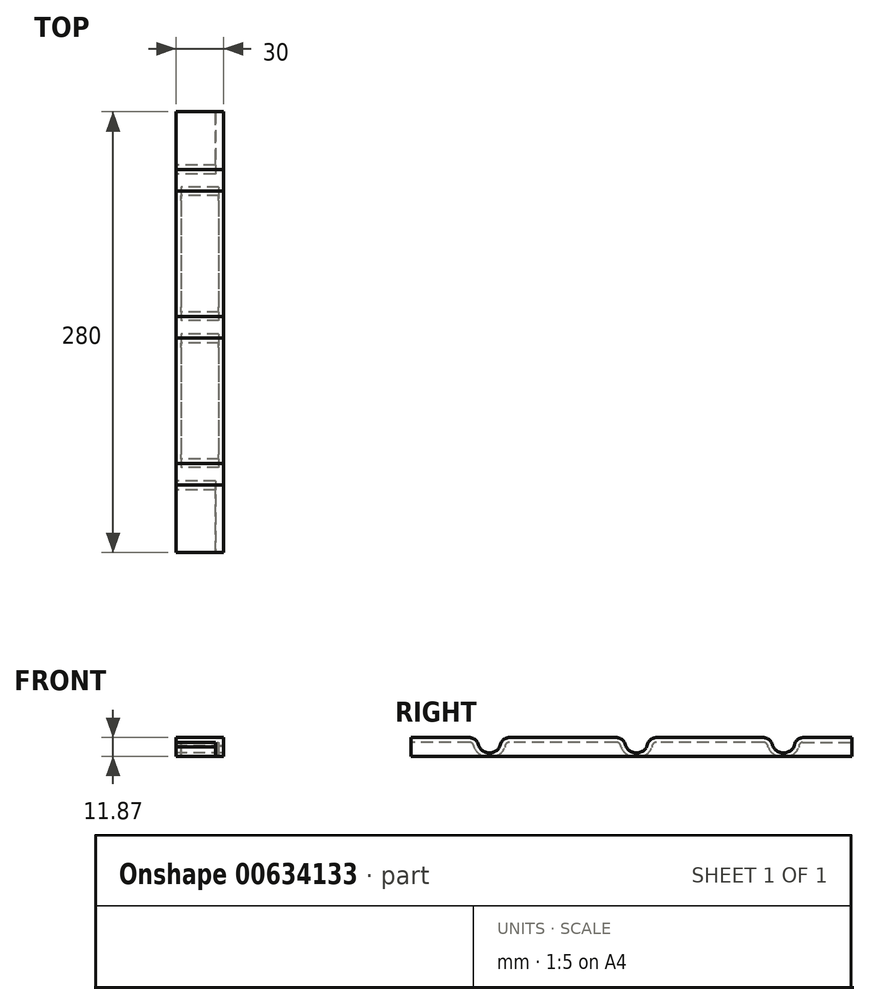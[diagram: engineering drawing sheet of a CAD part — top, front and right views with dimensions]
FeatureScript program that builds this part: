
annotation { "Feature Type Name" : "Feature", "Feature Type Description" : "" }
export const myFeature = defineFeature(function(context is Context, id is Id, definition is map)
    precondition{}
    {
        {
            var Q0;
            Q0=qCreatedBy(makeId("Front.planeOp"),FACE);
            var sketch = newSketch(context, id + "F0", { "sketchPlane" : qUnion([Q0])});
            skLineSegment(sketch, "E0.bottom", {"start": v(-15, 40) * mm, "end": v(15, 40) * mm});
            skLineSegment(sketch, "E0.top", {"start": v(-12, 0) * mm, "end": v(12, 0) * mm});
            skLineSegment(sketch, "E0.left", {"start": v(-15, 40) * mm, "end": v(-15, 37) * mm});
            skLineSegment(sketch, "E0.right", {"start": v(15, 37) * mm, "end": v(15, 3) * mm});
            skLineSegment(sketch, "E1.0", {"start": v(-15, 37) * mm, "end": v(3, 37) * mm});
            skLineSegment(sketch, "E1.1", {"start": v(-12, 6) * mm, "end": v(-12, 6) * mm});
            skLineSegment(sketch, "E1.2", {"start": v(-9, 3) * mm, "end": v(9, 3) * mm});
            skLineSegment(sketch, "E1.3", {"start": v(12, 29.6) * mm, "end": v(12, 6) * mm});
            skLineSegment(sketch, "E2.0", {"start": v(-15, 6) * mm, "end": v(-12, 6) * mm});
            skLineSegment(sketch, "E3", {"start": v(12, 40) * mm, "end": v(7.5, 40) * mm, "construction": true});
            skLineSegment(sketch, "E4", {"start": v(7, 34.8) * mm, "end": v(7, 40) * mm, "construction": true});
            skArc(sketch, "E5", {"start": v(7, 40) * mm, "mid": v(6.75, 29.6) * mm, "end": v(7.5, 39.98) * mm});
            skLineSegment(sketch, "E6.trimOffspring", {"start": v(-15, 6) * mm, "end": v(-15, 3) * mm});
            skPoint(sketch, "E7.orphan", {"position": v(5, 29.7) * mm});
            skPoint(sketch, "E8.visualSharp", {"position": v(15, 40) * mm});
            skArc(sketch, "E8.filletArc", {"start": v(15, 37) * mm, "mid": v(14.12, 39.12) * mm, "end": v(12, 40) * mm});
            skPoint(sketch, "E9.visualSharp", {"position": v(15, 0) * mm});
            skArc(sketch, "E9.filletArc", {"start": v(12, 0) * mm, "mid": v(14.12, 0.88) * mm, "end": v(15, 3) * mm});
            skArc(sketch, "E10.filletArc", {"start": v(9, 3) * mm, "mid": v(11.12, 3.88) * mm, "end": v(12, 6) * mm});
            skPoint(sketch, "E11.visualSharp", {"position": v(-12, 3) * mm});
            skArc(sketch, "E11.filletArc", {"start": v(-12, 6) * mm, "mid": v(-11.12, 3.88) * mm, "end": v(-9, 3) * mm});
            skPoint(sketch, "E12.visualSharp", {"position": v(-15, 0) * mm});
            skArc(sketch, "E12.filletArc", {"start": v(-15, 3) * mm, "mid": v(-14.12, 0.88) * mm, "end": v(-12, 0) * mm});
            skLineSegment(sketch, "E13.0", {"start": v(6.5, 34.8) * mm, "end": v(6.5, 39.8) * mm});
            skLineSegment(sketch, "E14.0", {"start": v(7.5, 34.8) * mm, "end": v(7.5, 40) * mm});
            skLineSegment(sketch, "E15", {"start": v(-15, 6) * mm, "end": v(-15, 16) * mm});
            skLineSegment(sketch, "E16", {"start": v(-15, 16) * mm, "end": v(-12, 16) * mm});
            skLineSegment(sketch, "E17", {"start": v(-12, 16) * mm, "end": v(-12, 6) * mm});
            skLineSegment(sketch, "E18", {"start": v(6.75, 29.6) * mm, "end": v(12, 29.6) * mm});
            skSolve(sketch);
        }
        {
            var Q0;
            Q0=qCreatedBy(makeId("Front.planeOp"),FACE);
            var sketch = newSketch(context, id + "F1", { "sketchPlane" : qUnion([Q0])});
            skArc(sketch, "E19.0.0", {"start": v(7.25, 29.6) * mm, "mid": v(12.2, 34.67) * mm, "end": v(7.5, 39.98) * mm});
            skLineSegment(sketch, "E19.0.1", {"start": v(7.5, 39.98) * mm, "end": v(7.5, 40) * mm});
            skArc(sketch, "E19.0.3", {"start": v(6.5, 39.98) * mm, "mid": v(4, 39.05) * mm, "end": v(2.29, 37) * mm});
            skArc(sketch, "E19.0.4", {"start": v(2.29, 37) * mm, "mid": v(2.55, 32.11) * mm, "end": v(6.75, 29.6) * mm});
            skLineSegment(sketch, "E19.0.5", {"start": v(6.75, 29.6) * mm, "end": v(7.25, 29.6) * mm});
            skArc(sketch, "E19.1.0", {"start": v(2.29, 37) * mm, "mid": v(4, 39.05) * mm, "end": v(6.5, 39.98) * mm});
            skLineSegment(sketch, "E19.1.1", {"start": v(6.5, 40) * mm, "end": v(-15, 40) * mm});
            skLineSegment(sketch, "E19.1.2", {"start": v(-15, 40) * mm, "end": v(-15, 37) * mm});
            skLineSegment(sketch, "E19.1.3", {"start": v(-15, 37) * mm, "end": v(-0.9, 37) * mm});
            skArc(sketch, "E19.2.0", {"start": v(7.5, 39.98) * mm, "mid": v(12.2, 34.67) * mm, "end": v(7.25, 29.6) * mm});
            skLineSegment(sketch, "E19.2.2", {"start": v(12, 26.6) * mm, "end": v(12, 25) * mm});
            skArc(sketch, "E19.2.3", {"start": v(12, 6) * mm, "mid": v(11.12, 3.88) * mm, "end": v(9, 3) * mm, "construction": true});
            skLineSegment(sketch, "E19.2.4", {"start": v(9, 3) * mm, "end": v(-9, 3) * mm, "construction": true});
            skArc(sketch, "E19.2.5", {"start": v(-9, 3) * mm, "mid": v(-11.12, 3.88) * mm, "end": v(-12, 6) * mm, "construction": true});
            skLineSegment(sketch, "E19.2.7", {"start": v(-15, 6) * mm, "end": v(-15, 3) * mm, "construction": true});
            skArc(sketch, "E19.2.8", {"start": v(-15, 3) * mm, "mid": v(-14.12, 0.88) * mm, "end": v(-12, 0) * mm, "construction": true});
            skLineSegment(sketch, "E19.2.9", {"start": v(-12, 0) * mm, "end": v(12, 0) * mm, "construction": true});
            skArc(sketch, "E19.2.10", {"start": v(12, 0) * mm, "mid": v(14.12, 0.88) * mm, "end": v(15, 3) * mm, "construction": true});
            skLineSegment(sketch, "E19.2.11", {"start": v(15, 22) * mm, "end": v(15, 37) * mm});
            skArc(sketch, "E19.2.12", {"start": v(15, 37) * mm, "mid": v(14.12, 39.12) * mm, "end": v(12, 40) * mm});
            skLineSegment(sketch, "E19.2.13", {"start": v(12, 40) * mm, "end": v(7.5, 40) * mm});
            skLineSegment(sketch, "E19.2.14", {"start": v(7.5, 40) * mm, "end": v(7.5, 39.98) * mm});
            skLineSegment(sketch, "E19.3.0", {"start": v(-15, 28.87) * mm, "end": v(-15, 20) * mm});
            skLineSegment(sketch, "E19.3.2", {"start": v(-12, 23) * mm, "end": v(-12, 28.87) * mm});
            skLineSegment(sketch, "E19.3.3", {"start": v(-12, 16) * mm, "end": v(-12, 16) * mm});
            skPoint(sketch, "E20.2", {"position": v(6.5, 37.3) * mm});
            skPoint(sketch, "E21.orphan", {"position": v(6.5, 39.8) * mm});
            skPoint(sketch, "E19.0.2.end.orphan", {"position": v(7, 40) * mm});
            skArc(sketch, "E22.0", {"start": v(-0.9, 37) * mm, "mid": v(0.38, 29.97) * mm, "end": v(6.69, 26.6) * mm});
            skLineSegment(sketch, "E23.0", {"start": v(9.25, 26.6) * mm, "end": v(12, 26.6) * mm});
            skLineSegment(sketch, "E24.0", {"start": v(6.69, 26.6) * mm, "end": v(9.25, 26.6) * mm});
            skPoint(sketch, "E25.orphan", {"position": v(12, 29.6) * mm});
            skLineSegment(sketch, "E26.trimOffspring", {"start": v(6.5, 39.98) * mm, "end": v(6.5, 40) * mm});
            skPoint(sketch, "E27.orphan", {"position": v(7.5, 34.8) * mm});
            skPoint(sketch, "E20.0.start.orphan", {"position": v(6.5, 34.8) * mm});
            skLineSegment(sketch, "E28", {"start": v(7, 20) * mm, "end": v(-9, 20) * mm});
            skPoint(sketch, "E28.endSnap0", {"position": v(15, 20) * mm});
            skLineSegment(sketch, "E29", {"start": v(-15, 28.87) * mm, "end": v(-12, 28.87) * mm});
            skPoint(sketch, "E30.orphan", {"position": v(-15.47, 20) * mm});
            skLineSegment(sketch, "E31.0", {"start": v(10, 17) * mm, "end": v(-12, 17) * mm});
            skPoint(sketch, "E32.visualSharp", {"position": v(12, 20) * mm});
            skArc(sketch, "E32.filletArc", {"start": v(7, 20) * mm, "mid": v(10.54, 21.46) * mm, "end": v(12, 25) * mm});
            skPoint(sketch, "E33.visualSharp", {"position": v(15, 17) * mm});
            skArc(sketch, "E33.filletArc", {"start": v(10, 17) * mm, "mid": v(13.54, 18.46) * mm, "end": v(15, 22) * mm});
            skPoint(sketch, "E34.visualSharp", {"position": v(-15, 16) * mm});
            skPoint(sketch, "E35.visualSharp", {"position": v(-12, 20) * mm});
            skArc(sketch, "E35.filletArc", {"start": v(-12, 23) * mm, "mid": v(-11.12, 20.88) * mm, "end": v(-9, 20) * mm});
            skPoint(sketch, "E36.visualSharp", {"position": v(-15, 17) * mm});
            skArc(sketch, "E36.filletArc", {"start": v(-15, 20) * mm, "mid": v(-14.12, 17.88) * mm, "end": v(-12, 17) * mm});
            skSolve(sketch);
        }
        {
            var Q0;
            Q0=qCreatedBy(makeId("Front.planeOp"),FACE);
            var sketch = newSketch(context, id + "F2", { "sketchPlane" : qUnion([Q0])});
            skLineSegment(sketch, "E37", {"start": v(-15, 28.87) * mm, "end": v(-45, 28.87) * mm});
            skLineSegment(sketch, "E38", {"start": v(-45, 28.87) * mm, "end": v(-45, 17) * mm});
            skLineSegment(sketch, "E39.0", {"start": v(-15, 17) * mm, "end": v(-45, 17) * mm});
            skPoint(sketch, "E40.orphan", {"position": v(-12, 17) * mm});
            skLineSegment(sketch, "E41", {"start": v(-15, 28.87) * mm, "end": v(-15, 17) * mm});
            skPoint(sketch, "E42.orphan", {"position": v(10, 17) * mm});
            skSolve(sketch);
        }
        {
            var Q0;
            Q0 = qSketchRegion(id + "F2", true);
            extrude(context, id + "F3", {"entities" : qUnion([Q0]), "oppositeDirection" : true, "depth" : 280 * mm, "offsetDistance" : 25 * mm});
        }
        {
            var Q0;
            Q0=makeQuery(id+"F3.opExtrude","SWEPT_FACE",FACE,{"disambiguationData":[OSD([sQuery(id+"F2.wireOp",EDGE,"E38")])]});
            var sketch = newSketch(context, id + "F4", { "sketchPlane" : qUnion([Q0])});
            skSolve(sketch);
        }
        {
            var Q0;
            {var subQ0=sQuery(id+"F2.wireOp",EDGE,"E38");Q0=makeQuery(id+"F4.imprint","IMPRINT",FACE,{"disambiguationData":[TD([[makeQuery(id+"F4.imprint","IMPRINT",EDGE,{"derivedFrom":makeQuery(id+"F3.opExtrude","CAP_EDGE",EDGE,{"disambiguationData":[OSD([subQ0])],"isStart":true})}),-1.0]])]});}
            var sketch = newSketch(context, id + "F5", { "sketchPlane" : qUnion([Q0])});
            skLineSegment(sketch, "E43.0", {"start": v(-280, 17) * mm, "end": v(0, 17) * mm, "construction": true});
            skLineSegment(sketch, "E44.0", {"start": v(-280, 24) * mm, "end": v(0, 24) * mm, "construction": true});
            skSolve(sketch);
        }
        {
            var Q0;
            {var subQ0=sQuery(id+"F2.wireOp",EDGE,"E38");Q0=makeQuery(id+"F4.imprint","IMPRINT",FACE,{"disambiguationData":[TD([[makeQuery(id+"F4.imprint","IMPRINT",EDGE,{"derivedFrom":makeQuery(id+"F3.opExtrude","CAP_EDGE",EDGE,{"disambiguationData":[OSD([subQ0])],"isStart":true})}),-1.0]])]});}
            var sketch = newSketch(context, id + "F6", { "sketchPlane" : qUnion([Q0])});
            skLineSegment(sketch, "E45", {"start": v(0, 16.97) * mm, "end": v(-42.76, 16.97) * mm, "construction": true});
            skLineSegment(sketch, "E46", {"start": v(-42.76, 16.97) * mm, "end": v(-42.76, 25.5) * mm, "construction": true});
            skLineSegment(sketch, "E47", {"start": v(-42.76, 25.5) * mm, "end": v(-56.43, 25.5) * mm, "construction": true});
            skLineSegment(sketch, "E48", {"start": v(-56.43, 25.5) * mm, "end": v(-56.43, 16.97) * mm, "construction": true});
            skArc(sketch, "E49", {"start": v(-42.76, 25.5) * mm, "mid": v(-49.6, 28.8) * mm, "end": v(-56.43, 25.5) * mm, "construction": true});
            skLineSegment(sketch, "E50", {"start": v(-42.76, 16.97) * mm, "end": v(-42.76, 7.64) * mm, "construction": true});
            skLineSegment(sketch, "E51", {"start": v(-42.76, 7.64) * mm, "end": v(-57.13, 7.64) * mm, "construction": true});
            skLineSegment(sketch, "E52", {"start": v(-57.13, 7.64) * mm, "end": v(-56.43, 16.97) * mm, "construction": true});
            skArc(sketch, "E53", {"start": v(-56.43, 23.23) * mm, "mid": v(-49.46, 19.13) * mm, "end": v(-42.76, 23.65) * mm});
            skLineSegment(sketch, "E54", {"start": v(-56.43, 23.23) * mm, "end": v(-56.43, 52.2) * mm});
            skLineSegment(sketch, "E55", {"start": v(-56.43, 52.2) * mm, "end": v(-42.76, 52.2) * mm});
            skLineSegment(sketch, "E56", {"start": v(-42.76, 52.2) * mm, "end": v(-42.76, 23.65) * mm});
            skArc(sketch, "E57.1.0.0", {"start": v(-149.83, 23.23) * mm, "mid": v(-142.86, 19.13) * mm, "end": v(-136.16, 23.65) * mm});
            skLineSegment(sketch, "E57.1.0.1", {"start": v(-136.16, 52.2) * mm, "end": v(-136.16, 23.65) * mm});
            skLineSegment(sketch, "E57.1.0.2", {"start": v(-149.83, 23.23) * mm, "end": v(-149.83, 52.2) * mm});
            skLineSegment(sketch, "E57.1.0.3", {"start": v(-149.83, 52.2) * mm, "end": v(-136.16, 52.2) * mm});
            skArc(sketch, "E57.2.0.0", {"start": v(-243.23, 23.23) * mm, "mid": v(-236.26, 19.13) * mm, "end": v(-229.56, 23.65) * mm});
            skLineSegment(sketch, "E57.2.0.1", {"start": v(-229.56, 52.2) * mm, "end": v(-229.56, 23.65) * mm});
            skLineSegment(sketch, "E57.2.0.2", {"start": v(-243.23, 23.23) * mm, "end": v(-243.23, 52.2) * mm});
            skLineSegment(sketch, "E57.2.0.3", {"start": v(-243.23, 52.2) * mm, "end": v(-229.56, 52.2) * mm});
            skLineSegment(sketch, "E57.direction1", {"start": v(-56.43, 23.23) * mm, "end": v(-149.83, 23.23) * mm, "construction": true});
            skSolve(sketch);
        }
        {
            var Q0;
            Q0 = qSketchRegion(id + "F6", true);
            extrude(context, id + "F7", {"entities" : qUnion([Q0]), "operationType" : NewBodyOperationType.REMOVE, "endBound" : BoundingType.THROUGH_ALL, "oppositeDirection" : true, "depth" : 25 * mm, "offsetDistance" : 25 * mm});
        }
        {
            var Q0;
            Q0=makeQuery(id+"F7.boolean.opBoolean","INTERSECT",EDGE,{"derivedFrom":[makeQuery(id+"F3.opExtrude","SWEPT_FACE",FACE,{"disambiguationData":[OSD([sQuery(id+"F2.wireOp",EDGE,"E37")])]}),makeQuery(id+"F7.opExtrude","SWEPT_FACE",FACE,{"disambiguationData":[OSD([sQuery(id+"F6.wireOp",EDGE,"E57.2.0.1")])]})]});
            var Q1;
            Q1=makeQuery(id+"F7.boolean.opBoolean","INTERSECT",EDGE,{"derivedFrom":[makeQuery(id+"F3.opExtrude","SWEPT_FACE",FACE,{"disambiguationData":[OSD([sQuery(id+"F2.wireOp",EDGE,"E37")])]}),makeQuery(id+"F7.opExtrude","SWEPT_FACE",FACE,{"disambiguationData":[OSD([sQuery(id+"F6.wireOp",EDGE,"E57.2.0.2")])]})]});
            var Q2;
            Q2=makeQuery(id+"F7.boolean.opBoolean","INTERSECT",EDGE,{"derivedFrom":[makeQuery(id+"F3.opExtrude","SWEPT_FACE",FACE,{"disambiguationData":[OSD([sQuery(id+"F2.wireOp",EDGE,"E37")])]}),makeQuery(id+"F7.opExtrude","SWEPT_FACE",FACE,{"disambiguationData":[OSD([sQuery(id+"F6.wireOp",EDGE,"E57.1.0.2")])]})]});
            var Q3;
            Q3=makeQuery(id+"F7.boolean.opBoolean","INTERSECT",EDGE,{"derivedFrom":[makeQuery(id+"F3.opExtrude","SWEPT_FACE",FACE,{"disambiguationData":[OSD([sQuery(id+"F2.wireOp",EDGE,"E37")])]}),makeQuery(id+"F7.opExtrude","SWEPT_FACE",FACE,{"disambiguationData":[OSD([sQuery(id+"F6.wireOp",EDGE,"E57.1.0.1")])]})]});
            var Q4;
            Q4=makeQuery(id+"F7.boolean.opBoolean","INTERSECT",EDGE,{"derivedFrom":[makeQuery(id+"F3.opExtrude","SWEPT_FACE",FACE,{"disambiguationData":[OSD([sQuery(id+"F2.wireOp",EDGE,"E37")])]}),makeQuery(id+"F7.opExtrude","SWEPT_FACE",FACE,{"disambiguationData":[OSD([sQuery(id+"F6.wireOp",EDGE,"E54")])]})]});
            var Q5;
            Q5=makeQuery(id+"F7.boolean.opBoolean","INTERSECT",EDGE,{"derivedFrom":[makeQuery(id+"F3.opExtrude","SWEPT_FACE",FACE,{"disambiguationData":[OSD([sQuery(id+"F2.wireOp",EDGE,"E37")])]}),makeQuery(id+"F7.opExtrude","SWEPT_FACE",FACE,{"disambiguationData":[OSD([sQuery(id+"F6.wireOp",EDGE,"E56")])]})]});
            fillet(context, id + "F8", {"entities" : qUnion([Q0, Q1, Q2, Q3, Q4, Q5]), "radius" : 6 * mm, "tangentPropagation" : true, "allowEdgeOverflow" : false});
        }
        {
            var Q0;
            {var subQ12=sQuery(id+"F6.wireOp",EDGE,"E53");Q0=makeQuery(id+"F6.imprint","IMPRINT",FACE,{"disambiguationData":[TD([[makeQuery(id+"F6.imprint","IMPRINT",EDGE,{"derivedFrom":subQ12}),-1.0]])]});}
            var sketch = newSketch(context, id + "F9", { "sketchPlane" : qUnion([Q0])});
            skLineSegment(sketch, "E58.0", {"start": v(-280, 28.87) * mm, "end": v(-249.22, 28.87) * mm, "construction": true});
            skLineSegment(sketch, "E59.0", {"start": v(-280, 25.87) * mm, "end": v(-249.22, 25.87) * mm});
            skArc(sketch, "E60.0", {"start": v(-246.13, 22.59) * mm, "mid": v(-246.93, 24.96) * mm, "end": v(-249.22, 25.97) * mm});
            skArc(sketch, "E60.1", {"start": v(-246.13, 22.59) * mm, "mid": v(-243.84, 19.23) * mm, "end": v(-240.46, 17) * mm});
            skLineSegment(sketch, "E61.0", {"start": v(-280, 17) * mm, "end": v(-240.46, 17) * mm});
            skPoint(sketch, "E62.trimOffspring.end.orphan", {"position": v(0, 17) * mm});
            skLineSegment(sketch, "E63", {"start": v(-280, 25.87) * mm, "end": v(-286.92, 25.87) * mm});
            skLineSegment(sketch, "E64", {"start": v(-286.92, 25.87) * mm, "end": v(-286.92, 17) * mm});
            skLineSegment(sketch, "E65", {"start": v(-286.92, 17) * mm, "end": v(-280, 17) * mm});
            skLineSegment(sketch, "E66.0", {"start": v(-36.82, 28.87) * mm, "end": v(0, 28.87) * mm, "construction": true});
            skLineSegment(sketch, "E67.0", {"start": v(-36.82, 25.87) * mm, "end": v(0, 25.87) * mm});
            skArc(sketch, "E68.0", {"start": v(-45.48, 17) * mm, "mid": v(-42.05, 19.4) * mm, "end": v(-39.81, 22.94) * mm});
            skArc(sketch, "E68.1", {"start": v(-36.82, 25.87) * mm, "mid": v(-38.91, 25.01) * mm, "end": v(-39.81, 22.94) * mm});
            skLineSegment(sketch, "E69", {"start": v(0, 17) * mm, "end": v(-45.48, 17) * mm});
            skLineSegment(sketch, "E70", {"start": v(0, 25.87) * mm, "end": v(7.4, 25.87) * mm});
            skLineSegment(sketch, "E71", {"start": v(7.4, 25.87) * mm, "end": v(8.77, 17) * mm});
            skLineSegment(sketch, "E72", {"start": v(8.77, 17) * mm, "end": v(0, 17) * mm});
            skSolve(sketch);
        }
        {
            var Q0;
            Q0 = qSketchRegion(id + "F9", true);
            extrude(context, id + "F10", {"entities" : qUnion([Q0]), "operationType" : NewBodyOperationType.REMOVE, "oppositeDirection" : true, "depth" : 25 * mm, "offsetDistance" : 25 * mm});
        }
        {
            var Q0;
            {var subQ12=sQuery(id+"F6.wireOp",EDGE,"E53");Q0=makeQuery(id+"F6.imprint","IMPRINT",FACE,{"disambiguationData":[TD([[makeQuery(id+"F6.imprint","IMPRINT",EDGE,{"derivedFrom":subQ12}),-1.0]])]});}
            var sketch = newSketch(context, id + "F11", { "sketchPlane" : qUnion([Q0])});
            skArc(sketch, "E73.0", {"start": v(-246.13, 22.59) * mm, "mid": v(-243.84, 19.23) * mm, "end": v(-240.46, 17) * mm});
            skArc(sketch, "E73.1", {"start": v(-246.13, 22.59) * mm, "mid": v(-246.67, 24.63) * mm, "end": v(-248.4, 25.86) * mm});
            skLineSegment(sketch, "E73.2", {"start": v(-280, 25.87) * mm, "end": v(-248.48, 25.87) * mm});
            skLineSegment(sketch, "E73.3.0", {"start": v(-286.92, 25.87) * mm, "end": v(-286.92, 17) * mm});
            skLineSegment(sketch, "E73.3.1", {"start": v(-286.92, 17) * mm, "end": v(-280, 17) * mm});
            skLineSegment(sketch, "E73.3.3", {"start": v(-280, 25.87) * mm, "end": v(-286.92, 25.87) * mm});
            skLineSegment(sketch, "E73.4", {"start": v(-280, 17) * mm, "end": v(-240.46, 17) * mm});
            skPoint(sketch, "E73.5", {"position": v(-243.84, 19.23) * mm});
            skPoint(sketch, "E73.6", {"position": v(-246.93, 24.96) * mm});
            skPoint(sketch, "E74.orphan", {"position": v(-249.22, 25.87) * mm});
            skPoint(sketch, "E75.orphan", {"position": v(-249.22, 25.97) * mm});
            skPoint(sketch, "E76.visualSharp", {"position": v(-248.44, 25.87) * mm});
            skArc(sketch, "E76.filletArc", {"start": v(-248.4, 25.86) * mm, "mid": v(-248.43, 25.86) * mm, "end": v(-248.48, 25.87) * mm});
            skSolve(sketch);
        }
        {
            var Q0;
            Q0 = qSketchRegion(id + "F11", true);
            extrude(context, id + "F12", {"entities" : qUnion([Q0]), "operationType" : NewBodyOperationType.REMOVE, "oppositeDirection" : true, "depth" : 25 * mm, "offsetDistance" : 25 * mm});
        }
        {
            var Q0;
            Q0=makeQuery(id+"F3.opExtrude","SWEPT_FACE",FACE,{"disambiguationData":[OSD([sQuery(id+"F2.wireOp",EDGE,"E39.0")])]});
            shell(context, id + "F13", {"entities" : qUnion([Q0]), "thickness" : 3 * mm});
        }
    });
